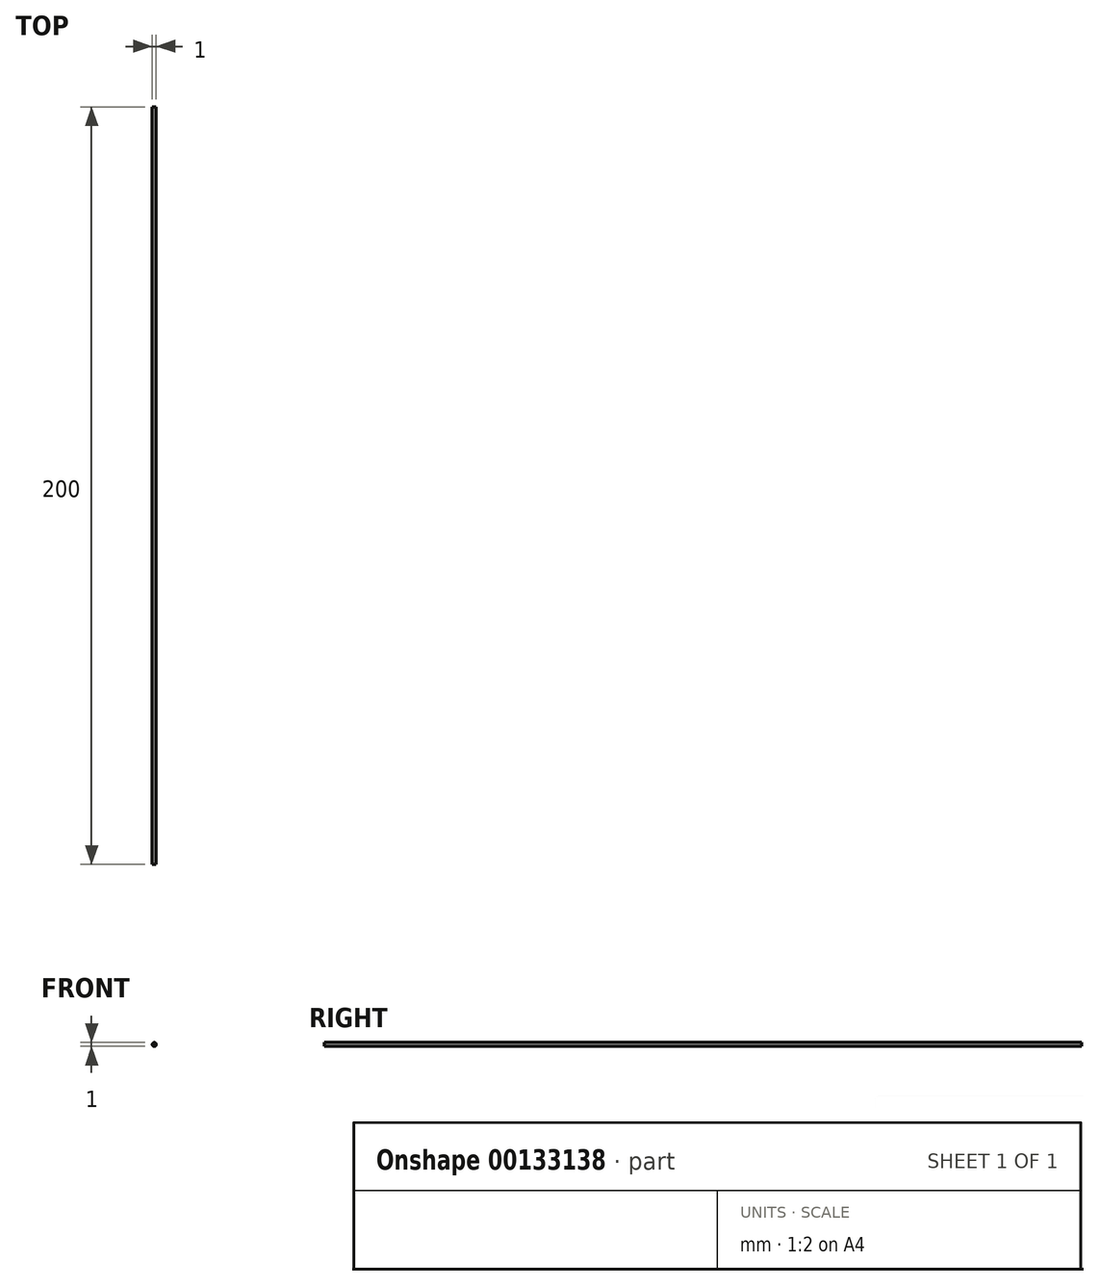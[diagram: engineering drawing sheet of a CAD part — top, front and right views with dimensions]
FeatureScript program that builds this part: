
annotation { "Feature Type Name" : "Feature", "Feature Type Description" : "" }
export const myFeature = defineFeature(function(context is Context, id is Id, definition is map)
    precondition{}
    {
        {
            var Q0;
            Q0=qCreatedBy(makeId("Front.planeOp"),FACE);
            var sketch = newSketch(context, id + "F0", { "sketchPlane" : qUnion([Q0])});
            skCircle(sketch, "E0", {"center": v(0, 0) * mm, "radius": 0.5 * mm});
            skSolve(sketch);
        }
        {
            var Q0;
            Q0=sQuery(id+"F0.wireOp",EDGE,"E0");
            extrude(context, id + "F1", {"bodyType" : ToolBodyType.SURFACE, "surfaceEntities" : qUnion([Q0]), "depth" : 200 * mm});
        }
    });
